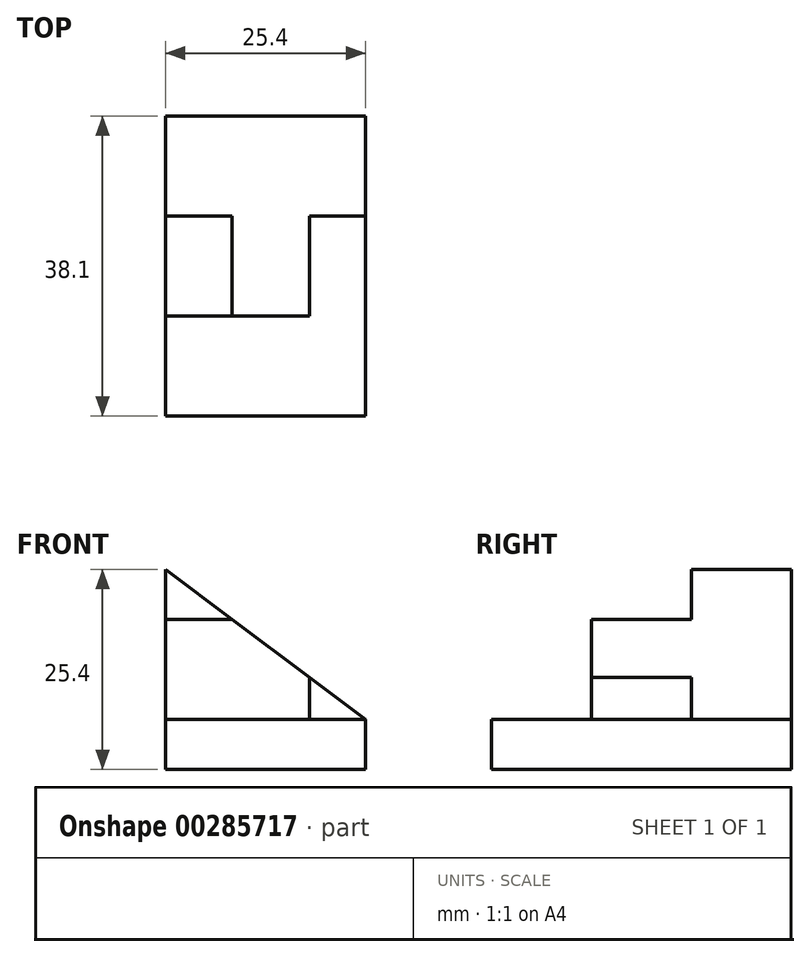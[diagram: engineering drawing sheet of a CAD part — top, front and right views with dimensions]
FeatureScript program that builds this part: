
annotation { "Feature Type Name" : "Feature", "Feature Type Description" : "" }
export const myFeature = defineFeature(function(context is Context, id is Id, definition is map)
    precondition{}
    {
        {
            var Q0;
            Q0=qCreatedBy(makeId("Front.planeOp"),FACE);
            var sketch = newSketch(context, id + "F0", { "sketchPlane" : qUnion([Q0])});
            skLineSegment(sketch, "E0.bottom", {"start": v(0, 0) * mm, "end": v(25.4, 0) * mm});
            skLineSegment(sketch, "E0.top", {"start": v(0, 6.35) * mm, "end": v(25.4, 6.35) * mm});
            skLineSegment(sketch, "E0.left", {"start": v(0, 0) * mm, "end": v(0, 6.35) * mm});
            skLineSegment(sketch, "E0.right", {"start": v(25.4, 0) * mm, "end": v(25.4, 6.35) * mm});
            skSolve(sketch);
        }
        {
            var Q0;
            Q0 = qSketchRegion(id + "F0", true);
            extrude(context, id + "F1", {"entities" : qUnion([Q0]), "oppositeDirection" : true, "depth" : 38.1 * mm});
        }
        {
            var Q0;
            Q0=makeQuery(id+"F1.opExtrude","CAP_FACE",FACE,{"disambiguationData":[OSD([sQuery(id+"F0.wireOp",EDGE,"E0.bottom"),sQuery(id+"F0.wireOp",EDGE,"E0.top"),sQuery(id+"F0.wireOp",EDGE,"E0.left"),sQuery(id+"F0.wireOp",EDGE,"E0.right")])],"isStart":true});
            cPlane(context, id + "F2", {"entities" : qUnion([Q0]), "cplaneType" : CPlaneType.OFFSET, "offset" : 12.7 * mm, "oppositeDirection" : true, "width" : 152.4 * mm, "height" : 152.4 * mm});
        }
        {
            var Q0;
            Q0=qCreatedBy(id+"F2.planeOp",FACE);
            var sketch = newSketch(context, id + "F3", { "sketchPlane" : qUnion([Q0])});
            skLineSegment(sketch, "E1", {"start": v(0, 6.35) * mm, "end": v(0, 25.4) * mm});
            skLineSegment(sketch, "E2", {"start": v(0, 25.4) * mm, "end": v(25.4, 6.35) * mm});
            skLineSegment(sketch, "E3", {"start": v(25.4, 6.35) * mm, "end": v(0, 6.35) * mm});
            skSolve(sketch);
        }
        {
            var Q0;
            Q0 = qSketchRegion(id + "F3", true);
            extrude(context, id + "F4", {"entities" : qUnion([Q0]), "operationType" : NewBodyOperationType.ADD, "oppositeDirection" : true, "depth" : 25.4 * mm});
        }
        {
            var Q0;
            Q0=makeQuery(id+"F4.opExtrude","CAP_FACE",FACE,{"disambiguationData":[OSD([sQuery(id+"F3.wireOp",EDGE,"E1"),sQuery(id+"F3.wireOp",EDGE,"E2"),sQuery(id+"F3.wireOp",EDGE,"E3")])],"isStart":true});
            var sketch = newSketch(context, id + "F5", { "sketchPlane" : qUnion([Q0])});
            skLineSegment(sketch, "E4", {"start": v(0, 25.4) * mm, "end": v(0, 19.05) * mm});
            skLineSegment(sketch, "E5", {"start": v(0, 19.05) * mm, "end": v(8.47, 19.05) * mm});
            skLineSegment(sketch, "E6", {"start": v(8.47, 19.05) * mm, "end": v(0, 25.4) * mm});
            skLineSegment(sketch, "E7", {"start": v(25.4, 6.35) * mm, "end": v(18.29, 6.35) * mm});
            skLineSegment(sketch, "E8", {"start": v(18.29, 6.35) * mm, "end": v(18.29, 11.68) * mm});
            skLineSegment(sketch, "E9", {"start": v(18.29, 11.68) * mm, "end": v(25.4, 6.35) * mm});
            skSolve(sketch);
        }
        {
            var Q0;
            Q0 = qSketchRegion(id + "F5", true);
            extrude(context, id + "F6", {"entities" : qUnion([Q0]), "operationType" : NewBodyOperationType.REMOVE, "oppositeDirection" : true, "depth" : 12.7 * mm});
        }
    });
